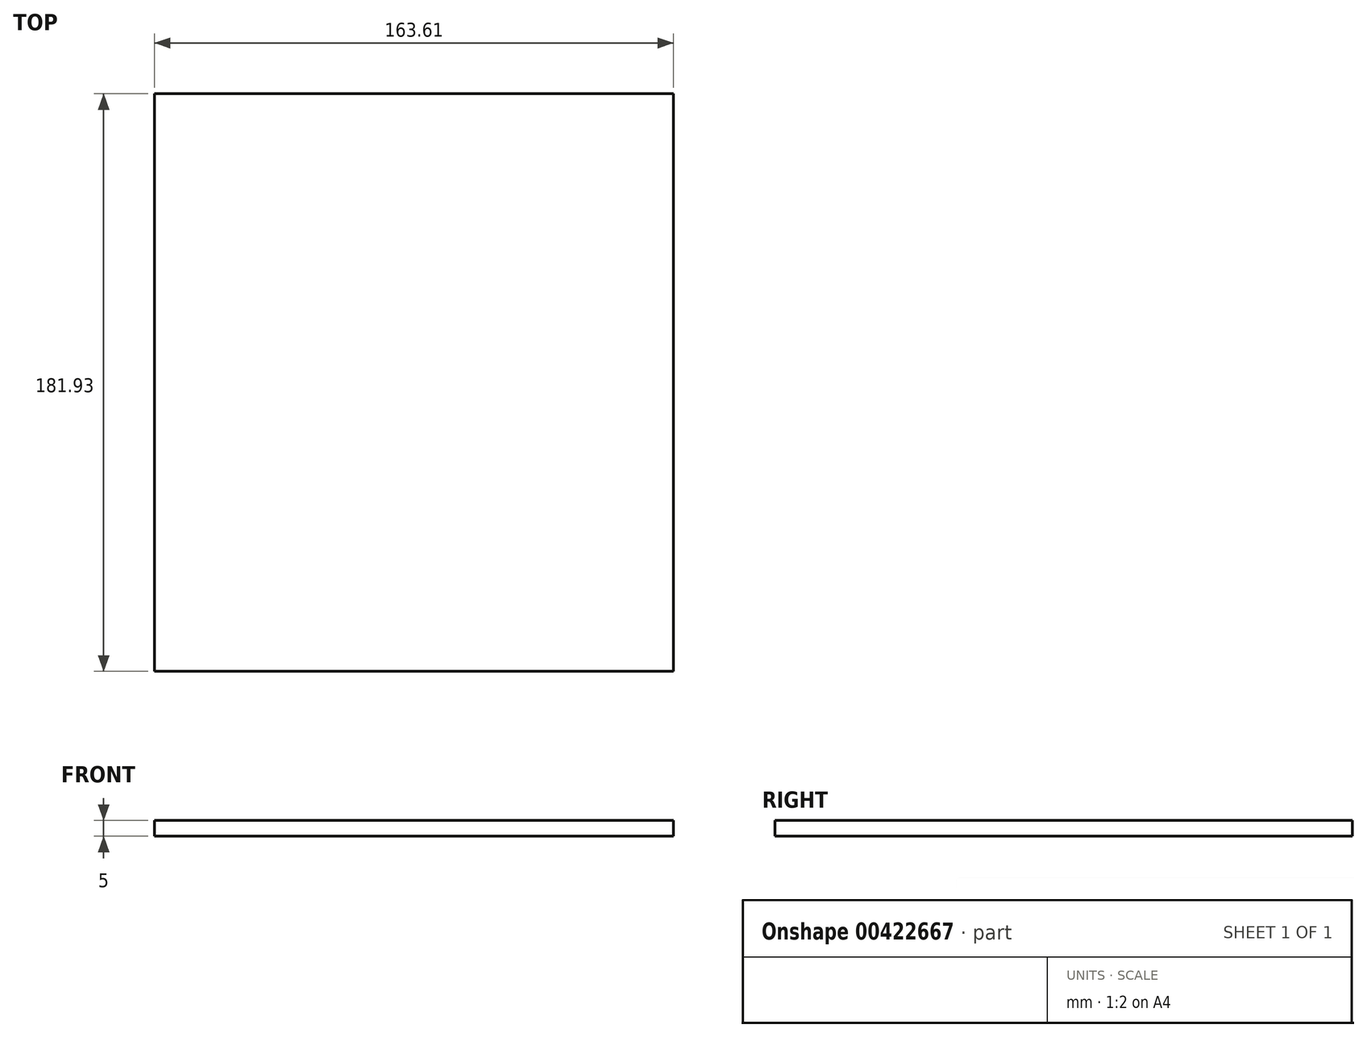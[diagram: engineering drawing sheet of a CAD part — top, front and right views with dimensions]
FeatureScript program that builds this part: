
annotation { "Feature Type Name" : "Feature", "Feature Type Description" : "" }
export const myFeature = defineFeature(function(context is Context, id is Id, definition is map)
    precondition{}
    {
        {
            var Q0;
            Q0=qCreatedBy(makeId("Top.planeOp"),FACE);
            var sketch = newSketch(context, id + "F0", { "sketchPlane" : qUnion([Q0])});
            skLineSegment(sketch, "E0", {"start": v(57.34, -28.54) * mm, "end": v(-106.27, -28.54) * mm});
            skLineSegment(sketch, "E1", {"start": v(57.34, -28.54) * mm, "end": v(13.05, -28.54) * mm});
            skLineSegment(sketch, "E2", {"start": v(57.34, -28.54) * mm, "end": v(57.34, 153.39) * mm});
            skLineSegment(sketch, "E3", {"start": v(-106.27, -28.54) * mm, "end": v(-106.27, 153.39) * mm});
            skLineSegment(sketch, "E4", {"start": v(-106.27, 153.39) * mm, "end": v(57.34, 153.39) * mm});
            skSolve(sketch);
        }
        {
            var Q0;
            Q0 = qSketchRegion(id + "F0", true);
            extrude(context, id + "F1", {"entities" : qUnion([Q0]), "depth" : 5 * mm});
        }
    });
